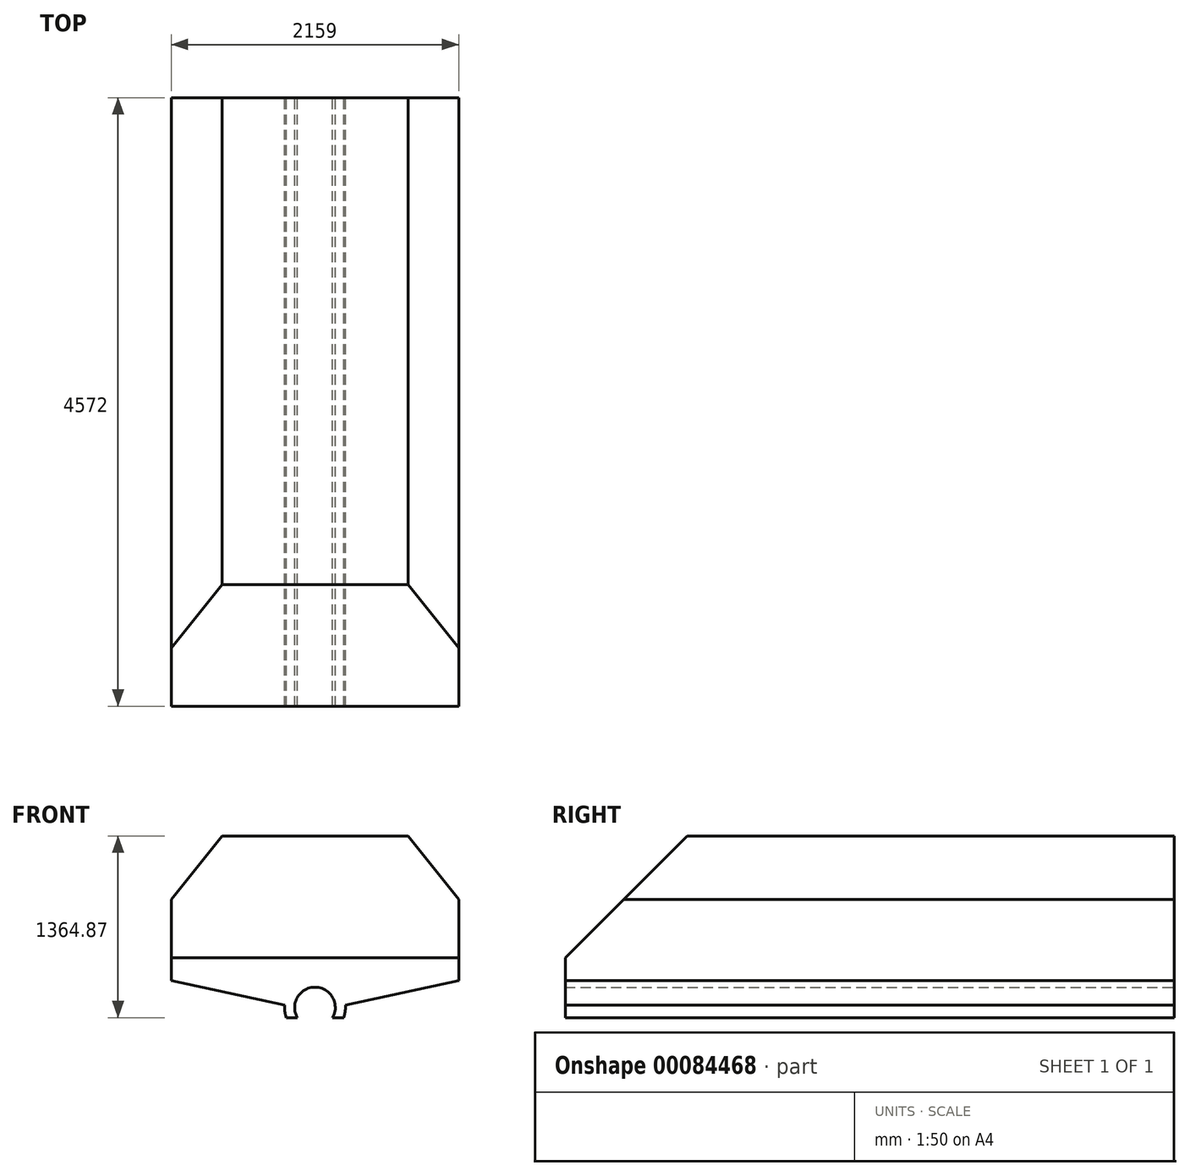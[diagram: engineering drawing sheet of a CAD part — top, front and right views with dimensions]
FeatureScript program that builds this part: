
annotation { "Feature Type Name" : "Feature", "Feature Type Description" : "" }
export const myFeature = defineFeature(function(context is Context, id is Id, definition is map)
    precondition{}
    {
        {
            var Q0;
            Q0=qCreatedBy(makeId("Front.planeOp"),FACE);
            var sketch = newSketch(context, id + "F0", { "sketchPlane" : qUnion([Q0])});
            skCircle(sketch, "E0", {"center": v(0, 0) * mm, "radius": 152.4 * mm});
            skLineSegment(sketch, "E1", {"start": v(-152.4, 0) * mm, "end": v(-152.4, 508) * mm});
            skLineSegment(sketch, "E2", {"start": v(-152.4, 508) * mm, "end": v(152.4, 508) * mm});
            skLineSegment(sketch, "E3", {"start": v(152.4, 508) * mm, "end": v(152.4, 0) * mm});
            skLineSegment(sketch, "E4.bottom", {"start": v(-1079.5, 812.8) * mm, "end": v(1079.5, 812.8) * mm});
            skLineSegment(sketch, "E4.top", {"start": v(-1079.5, 203.2) * mm, "end": v(1079.5, 203.2) * mm});
            skLineSegment(sketch, "E4.left", {"start": v(-1079.5, 812.8) * mm, "end": v(-1079.5, 203.2) * mm});
            skLineSegment(sketch, "E4.right", {"start": v(1079.5, 812.8) * mm, "end": v(1079.5, 203.2) * mm});
            skPoint(sketch, "E4.middle", {"position": v(0, 508) * mm});
            skLineSegment(sketch, "E5", {"start": v(-1079.5, 812.8) * mm, "end": v(-698.5, 1288.67) * mm});
            skLineSegment(sketch, "E6", {"start": v(-698.5, 1288.67) * mm, "end": v(698.5, 1288.67) * mm});
            skLineSegment(sketch, "E7", {"start": v(698.5, 1288.67) * mm, "end": v(1079.5, 812.8) * mm});
            skLineSegment(sketch, "E8", {"start": v(-1079.5, 203.2) * mm, "end": v(-152.4, 0) * mm});
            skLineSegment(sketch, "E9", {"start": v(1079.5, 203.2) * mm, "end": v(152.4, 0) * mm});
            skArc(sketch, "E10", {"start": v(-228, 16.57) * mm, "mid": v(0, -228.6) * mm, "end": v(228, 16.57) * mm});
            skLineSegment(sketch, "E11", {"start": v(357.85, 0) * mm, "end": v(-505.6, 0) * mm, "construction": true});
            skLineSegment(sketch, "E12", {"start": v(-215.53, -76.2) * mm, "end": v(215.53, -76.2) * mm});
            skSolve(sketch);
        }
        {
            var Q0;
            Q0=makeQuery(id+"F0.imprint","IMPRINT",FACE,{"disambiguationData":[TD([[makeQuery(id+"F0.imprint","IMPRINT",EDGE,{"derivedFrom":sQuery(id+"F0.wireOp",EDGE,"E4.bottom")}),1.0]])]});
            var Q1;
            {var subQ1=sQuery(id+"F0.wireOp",EDGE,"E2");Q1=makeQuery(id+"F0.imprint","IMPRINT",FACE,{"disambiguationData":[TD([[makeQuery(id+"F0.imprint","IMPRINT",EDGE,{"derivedFrom":subQ1}),1.0]])]});}
            var Q2;
            {var subQ0=sQuery(id+"F0.wireOp",EDGE,"E2");Q2=makeQuery(id+"F0.imprint","IMPRINT",FACE,{"disambiguationData":[TD([[makeQuery(id+"F0.imprint","IMPRINT",EDGE,{"derivedFrom":subQ0}),-1.0]])]});}
            var Q3;
            {var subQ1=sQuery(id+"F0.wireOp",EDGE,"E1");var subQ3=sQuery(id+"F0.wireOp",EDGE,"E4.top");var subQ4=makeQuery(id+"F0.imprint","INTERSECT",VERTEX,{"derivedFrom":[subQ1,subQ3]});Q3=makeQuery(id+"F0.imprint","IMPRINT",FACE,{"disambiguationData":[TD([[makeQuery(id+"F0.imprint","IMPRINT",EDGE,{"disambiguationData":[TD([[subQ4,1.0]])],"derivedFrom":subQ1}),1.0]])]});}
            var Q4;
            {var subQ0=sQuery(id+"F0.wireOp",EDGE,"E1");var subQ5=sQuery(id+"F0.wireOp",EDGE,"E4.top");var subQ6=makeQuery(id+"F0.imprint","INTERSECT",VERTEX,{"derivedFrom":[subQ0,subQ5]});Q4=makeQuery(id+"F0.imprint","IMPRINT",FACE,{"disambiguationData":[TD([[makeQuery(id+"F0.imprint","IMPRINT",EDGE,{"disambiguationData":[TD([[subQ6,-1.0]])],"derivedFrom":subQ5}),-1.0]])]});}
            var Q5;
            {var subQ1=sQuery(id+"F0.wireOp",EDGE,"E3");var subQ3=sQuery(id+"F0.wireOp",EDGE,"E4.top");var subQ4=makeQuery(id+"F0.imprint","INTERSECT",VERTEX,{"derivedFrom":[subQ1,subQ3]});Q5=makeQuery(id+"F0.imprint","IMPRINT",FACE,{"disambiguationData":[TD([[makeQuery(id+"F0.imprint","IMPRINT",EDGE,{"disambiguationData":[TD([[subQ4,-1.0]])],"derivedFrom":subQ1}),1.0]])]});}
            var Q6;
            {var subQ0=sQuery(id+"F0.wireOp",EDGE,"E8");var subQ5=sQuery(id+"F0.wireOp",EDGE,"E10");var subQ6=makeQuery(id+"F0.imprint","INTERSECT",VERTEX,{"derivedFrom":[subQ0,subQ5]});Q6=makeQuery(id+"F0.imprint","IMPRINT",FACE,{"disambiguationData":[TD([[makeQuery(id+"F0.imprint","IMPRINT",EDGE,{"disambiguationData":[TD([[subQ6,-1.0]])],"derivedFrom":subQ5}),1.0]])]});}
            var Q7;
            {var subQ0=sQuery(id+"F0.wireOp",EDGE,"E9");var subQ5=sQuery(id+"F0.wireOp",EDGE,"E10");var subQ6=makeQuery(id+"F0.imprint","INTERSECT",VERTEX,{"derivedFrom":[subQ0,subQ5]});Q7=makeQuery(id+"F0.imprint","IMPRINT",FACE,{"disambiguationData":[TD([[makeQuery(id+"F0.imprint","IMPRINT",EDGE,{"disambiguationData":[TD([[subQ6,1.0]])],"derivedFrom":subQ5}),1.0]])]});}
            extrude(context, id + "F1", {"entities" : qUnion([Q0, Q1, Q2, Q3, Q4, Q5, Q6, Q7]), "depth" : 4572 * mm});
        }
        {
            var Q0;
            Q0=makeQuery(id+"F1.opExtrude","CAP_EDGE",EDGE,{"disambiguationData":[OSD([sQuery(id+"F0.wireOp",EDGE,"E6")])],"isStart":false});
            chamfer(context, id + "F2", {"entities" : qUnion([Q0]), "width" : 914.4 * mm, "tangentPropagation" : true});
        }
    });
